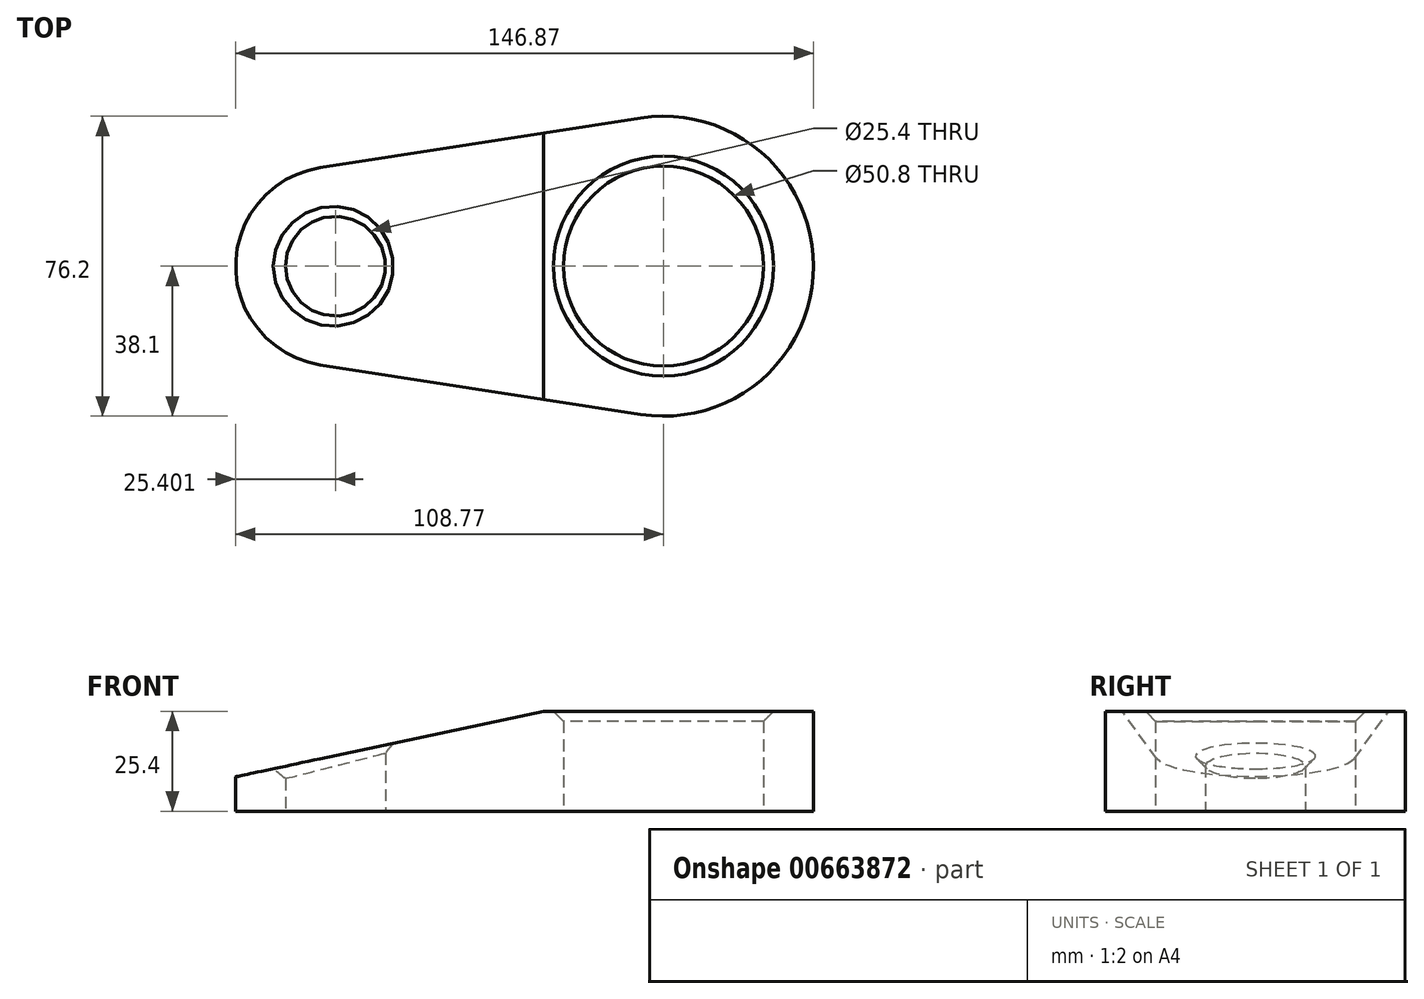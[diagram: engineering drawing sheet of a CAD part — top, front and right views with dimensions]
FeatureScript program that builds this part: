
annotation { "Feature Type Name" : "Feature", "Feature Type Description" : "" }
export const myFeature = defineFeature(function(context is Context, id is Id, definition is map)
    precondition{}
    {
        {
            var Q0;
            Q0=qCreatedBy(makeId("Top.planeOp"),FACE);
            var sketch = newSketch(context, id + "F0", { "sketchPlane" : qUnion([Q0])});
            skCircle(sketch, "E0", {"center": v(0, 0) * mm, "radius": 38.1 * mm});
            skCircle(sketch, "E1", {"center": v(-83.37, 0) * mm, "radius": 12.7 * mm});
            skCircle(sketch, "E2", {"center": v(0, 0) * mm, "radius": 25.4 * mm});
            skCircle(sketch, "E3", {"center": v(-83.37, 0) * mm, "radius": 25.4 * mm});
            skLineSegment(sketch, "E4", {"start": v(-87.24, 25.1) * mm, "end": v(-5.8, 37.66) * mm});
            skLineSegment(sketch, "E5", {"start": v(-87.24, -25.1) * mm, "end": v(-5.8, -37.66) * mm});
            skSolve(sketch);
        }
        {
            var Q0;
            Q0=makeQuery(id+"F0.imprint","IMPRINT",FACE,{"disambiguationData":[TD([[makeQuery(id+"F0.imprint","IMPRINT",EDGE,{"derivedFrom":sQuery(id+"F0.wireOp",EDGE,"E1")}),-1.0]])]});
            var Q1;
            Q1=makeQuery(id+"F0.imprint","IMPRINT",FACE,{"disambiguationData":[TD([[makeQuery(id+"F0.imprint","IMPRINT",EDGE,{"derivedFrom":sQuery(id+"F0.wireOp",EDGE,"E2")}),-1.0]])]});
            var Q2;
            {var subQ0=sQuery(id+"F0.wireOp",EDGE,"E4");Q2=makeQuery(id+"F0.imprint","IMPRINT",FACE,{"disambiguationData":[TD([[makeQuery(id+"F0.imprint","IMPRINT",EDGE,{"derivedFrom":subQ0}),-1.0]])]});}
            extrude(context, id + "F1", {"entities" : qUnion([Q0, Q1, Q2]), "depth" : 25.4 * mm, "offsetDistance" : 25.4 * mm});
        }
        {
            var Q0;
            Q0=qCreatedBy(makeId("Front.planeOp"),FACE);
            var sketch = newSketch(context, id + "F2", { "sketchPlane" : qUnion([Q0])});
            skLineSegment(sketch, "E6", {"start": v(0, 0) * mm, "end": v(0, 25.4) * mm, "construction": true});
            skLineSegment(sketch, "E7", {"start": v(-30.48, 25.4) * mm, "end": v(-128.31, 25.4) * mm});
            skLineSegment(sketch, "E8", {"start": v(-128.31, 25.4) * mm, "end": v(-128.31, 4.6) * mm});
            skLineSegment(sketch, "E9", {"start": v(-128.31, 4.6) * mm, "end": v(-30.48, 25.4) * mm});
            skSolve(sketch);
        }
        {
            var Q0;
            Q0 = qSketchRegion(id + "F2", true);
            extrude(context, id + "F3", {"entities" : qUnion([Q0]), "operationType" : NewBodyOperationType.REMOVE, "endBound" : BoundingType.SYMMETRIC, "depth" : 115.32 * mm, "offsetDistance" : 25.4 * mm});
        }
        {
            var Q0;
            Q0=makeQuery(id+"F3.boolean.opBoolean","INTERSECT",EDGE,{"derivedFrom":[makeQuery(id+"F1.opExtrude","SWEPT_FACE",FACE,{"disambiguationData":[OSD([sQuery(id+"F0.wireOp",EDGE,"E1")])]}),makeQuery(id+"F3.opExtrude","SWEPT_FACE",FACE,{"disambiguationData":[OSD([sQuery(id+"F2.wireOp",EDGE,"E9")])]})]});
            var Q1;
            Q1=makeQuery(id+"F1.opExtrude","CAP_EDGE",EDGE,{"disambiguationData":[OSD([sQuery(id+"F0.wireOp",EDGE,"E2")])],"isStart":false});
            chamfer(context, id + "F4", {"entities" : qUnion([Q0, Q1]), "width" : 2.54 * mm, "tangentPropagation" : true});
        }
    });
